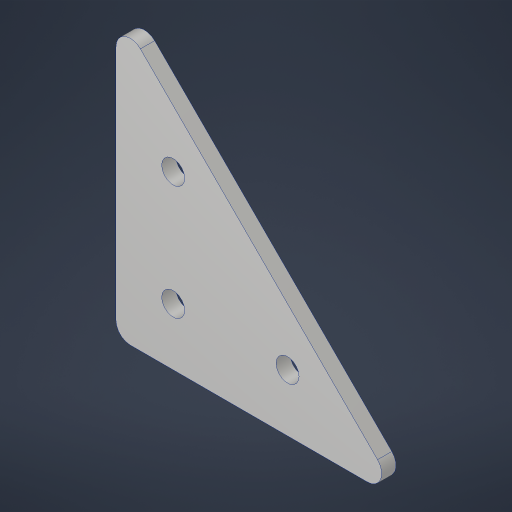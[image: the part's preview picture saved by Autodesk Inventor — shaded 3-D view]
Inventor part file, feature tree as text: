
AUTODESK INVENTOR PART (.ipt)
format: ipt  version: 2023.4 (Build 274418000, 418)  size: 189,952 bytes
history: native  units: in
note: dims shown in document units (in); Inventor stores cm internally (conversion verified against a paired STEP export)
features: pattern_linear x2, sketch x2, extrude x1, fillet x1, hole x1, projected_geometry x1
ambient origin geometry x8: Origin, YZ Plane, XZ Plane, XY Plane, X Axis, Y Axis, Z Axis, Center Point
bodies: Solid1 (feature_tree)
feature tree (8):
  extrude  "Extrusion1"  Depth=2.5in
  fillet  "Fillet1"  Radius=0.125in
  hole  "Hole1"  [1 undecoded]
  pattern_linear  "Rectangular Pattern1"  Spacing1=0.5in  [1 undecoded]
  pattern_linear  "Rectangular Pattern2"  Count1=2 Spacing1=1.0in
  sketch  "Sketch1"  dims[d0=2.5in d1=2.5in d2=0.125in d3=0.0in]
  sketch  "Sketch2"  dims[d4=0.125in d5=0.5in d6=0.5in d7=0.201in d8=0.75in d9=0.385in d10=0.25in d11=0.5635in d12=1.0in d13=0.8108in d14=0.7874in d16=1.0in d17=0.7874in d19=1.0in]
  projected_geometry  "Project Cut Edges1"
note: 2 required parameter values undecoded (feature->parameter linkage not recoverable at this tier; creation-order binding heuristic only, values carry confidence <= 0.55)
